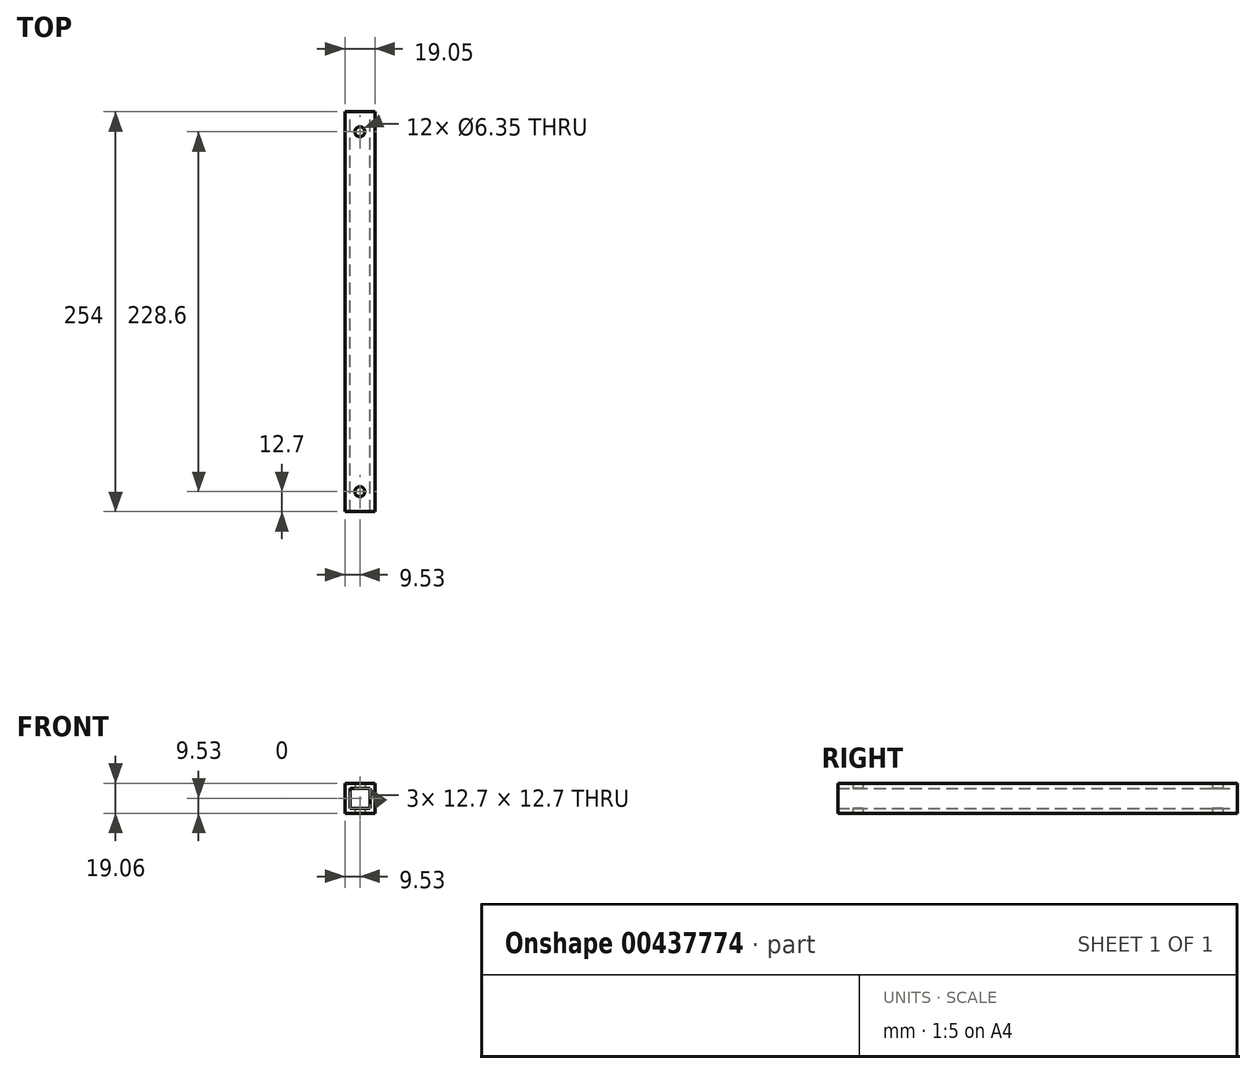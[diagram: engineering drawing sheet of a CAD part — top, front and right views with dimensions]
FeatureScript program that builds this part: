
annotation { "Feature Type Name" : "Feature", "Feature Type Description" : "" }
export const myFeature = defineFeature(function(context is Context, id is Id, definition is map)
    precondition{}
    {
        {
            var Q0;
            Q0=qCreatedBy(makeId("Front.planeOp"),FACE);
            var sketch = newSketch(context, id + "F0", { "sketchPlane" : qUnion([Q0])});
            skLineSegment(sketch, "E0.bottom", {"start": v(-15.88, 15.88) * mm, "end": v(3.17, 15.88) * mm});
            skLineSegment(sketch, "E0.top", {"start": v(-15.88, -3.18) * mm, "end": v(3.18, -3.18) * mm});
            skLineSegment(sketch, "E0.left", {"start": v(-15.88, 15.88) * mm, "end": v(-15.88, -3.18) * mm});
            skLineSegment(sketch, "E0.right", {"start": v(3.17, 15.88) * mm, "end": v(3.18, -3.18) * mm});
            skLineSegment(sketch, "E1.bottom", {"start": v(-12.7, 12.7) * mm, "end": v(0, 12.7) * mm});
            skLineSegment(sketch, "E1.top", {"start": v(-12.7, 0) * mm, "end": v(0, 0) * mm});
            skLineSegment(sketch, "E1.left", {"start": v(-12.7, 12.7) * mm, "end": v(-12.7, 0) * mm});
            skLineSegment(sketch, "E1.right", {"start": v(0, 12.7) * mm, "end": v(0, 0) * mm});
            skSolve(sketch);
        }
        {
            var Q0;
            Q0=qSketchRegion(id+"F0",true);
            extrude(context, id + "F1", {"entities" : qUnion([Q0]), "depth" : 254 * mm});
        }
        {
            var Q0;
            Q0=qCreatedBy(makeId("Top.planeOp"),FACE);
            var sketch = newSketch(context, id + "F2", { "sketchPlane" : qUnion([Q0])});
            skCircle(sketch, "E2", {"center": v(-6.35, -12.7) * mm, "radius": 3.17 * mm});
            skCircle(sketch, "E3", {"center": v(-6.35, -241.3) * mm, "radius": 3.18 * mm});
            skSolve(sketch);
        }
        {
            var Q0;
            Q0=qSketchRegion(id+"F2",true);
            extrude(context, id + "F3", {"entities" : qUnion([Q0]), "operationType" : NewBodyOperationType.REMOVE, "depth" : 127 * mm, "symmetric" : true});
        }
    });
